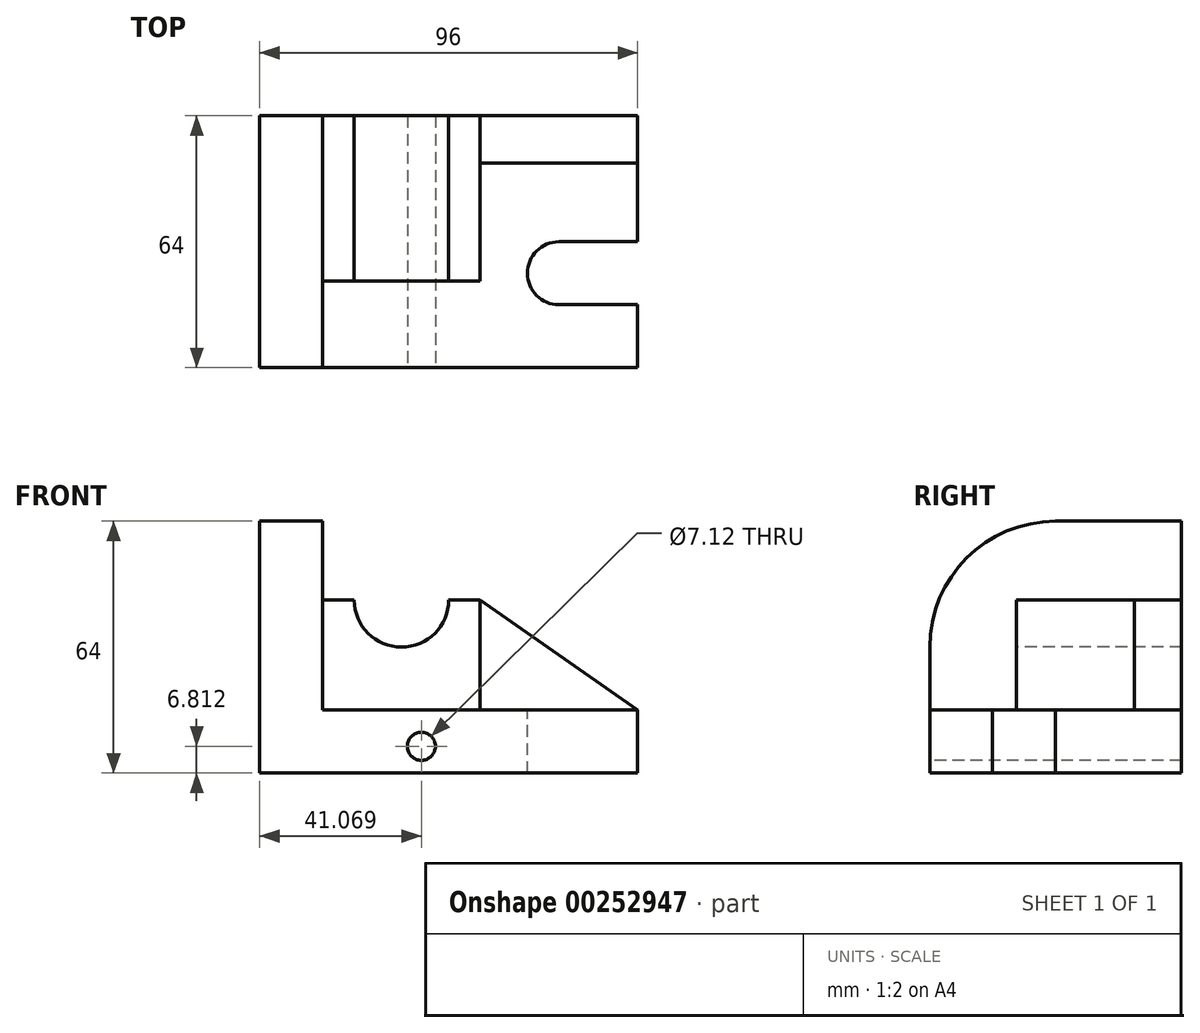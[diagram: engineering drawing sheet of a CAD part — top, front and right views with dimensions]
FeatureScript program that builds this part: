
annotation { "Feature Type Name" : "Feature", "Feature Type Description" : "" }
export const myFeature = defineFeature(function(context is Context, id is Id, definition is map)
    precondition{}
    {
        {
            var Q0;
            Q0=qCreatedBy(makeId("Top.planeOp"),FACE);
            var sketch = newSketch(context, id + "F0", { "sketchPlane" : qUnion([Q0])});
            skLineSegment(sketch, "E0.bottom", {"start": v(0, 0) * mm, "end": v(96, 0) * mm});
            skLineSegment(sketch, "E0.top", {"start": v(0, 64) * mm, "end": v(96, 64) * mm});
            skLineSegment(sketch, "E0.left", {"start": v(0, 0) * mm, "end": v(0, 64) * mm});
            skLineSegment(sketch, "E0.right", {"start": v(96, 0) * mm, "end": v(96, 64) * mm});
            skSolve(sketch);
        }
        {
            var Q0;
            Q0=makeQuery(id+"F0.imprint","IMPRINT",FACE,{"disambiguationData":[TD([[makeQuery(id+"F0.imprint","IMPRINT",EDGE,{"derivedFrom":sQuery(id+"F0.wireOp",EDGE,"E0.bottom")}),1.0]])]});
            extrude(context, id + "F1", {"entities" : qUnion([Q0]), "depth" : 16 * mm});
        }
        {
            var Q0;
            Q0=makeQuery(id+"F1.opExtrude","CAP_FACE",FACE,{"disambiguationData":[OSD([sQuery(id+"F0.wireOp",EDGE,"E0.bottom"),sQuery(id+"F0.wireOp",EDGE,"E0.top"),sQuery(id+"F0.wireOp",EDGE,"E0.left"),sQuery(id+"F0.wireOp",EDGE,"E0.right")])],"isStart":false});
            var sketch = newSketch(context, id + "F2", { "sketchPlane" : qUnion([Q0])});
            skLineSegment(sketch, "E1.0", {"start": v(76, 16) * mm, "end": v(96, 16) * mm});
            skLineSegment(sketch, "E2.0", {"start": v(76, 32) * mm, "end": v(96, 32) * mm});
            skArc(sketch, "E3", {"start": v(76, 32) * mm, "mid": v(68, 24) * mm, "end": v(76, 16) * mm});
            skLineSegment(sketch, "E4", {"start": v(96, 32) * mm, "end": v(96, 16) * mm});
            skSolve(sketch);
        }
        {
            var Q0;
            Q0=makeQuery(id+"F2.imprint","IMPRINT",FACE,{"disambiguationData":[TD([[makeQuery(id+"F2.imprint","IMPRINT",EDGE,{"derivedFrom":sQuery(id+"F2.wireOp",EDGE,"E1.0")}),1.0]])]});
            extrude(context, id + "F3", {"entities" : qUnion([Q0]), "operationType" : NewBodyOperationType.REMOVE, "endBound" : BoundingType.THROUGH_ALL, "oppositeDirection" : true, "depth" : 25.4 * mm});
        }
        {
            var Q0;
            Q0=makeQuery(id+"F1.opExtrude","CAP_FACE",FACE,{"disambiguationData":[OSD([sQuery(id+"F0.wireOp",EDGE,"E0.bottom"),sQuery(id+"F0.wireOp",EDGE,"E0.top"),sQuery(id+"F0.wireOp",EDGE,"E0.left"),sQuery(id+"F0.wireOp",EDGE,"E0.right")])],"isStart":false});
            var sketch = newSketch(context, id + "F4", { "sketchPlane" : qUnion([Q0])});
            skLineSegment(sketch, "E5.bottom", {"start": v(0, 0) * mm, "end": v(16, 0) * mm});
            skLineSegment(sketch, "E5.top", {"start": v(0, 64) * mm, "end": v(16, 64) * mm});
            skLineSegment(sketch, "E5.left", {"start": v(0, 0) * mm, "end": v(0, 64) * mm});
            skLineSegment(sketch, "E5.right", {"start": v(16, 0) * mm, "end": v(16, 64) * mm});
            skSolve(sketch);
        }
        {
            var Q0;
            Q0=makeQuery(id+"F4.imprint","IMPRINT",FACE,{"disambiguationData":[TD([[makeQuery(id+"F4.imprint","IMPRINT",EDGE,{"derivedFrom":sQuery(id+"F4.wireOp",EDGE,"E5.bottom")}),1.0]])]});
            extrude(context, id + "F5", {"entities" : qUnion([Q0]), "operationType" : NewBodyOperationType.ADD, "depth" : 48 * mm});
        }
        {
            var Q0;
            Q0=makeQuery(id+"F5.opExtrude","CAP_EDGE",EDGE,{"disambiguationData":[OSD([sQuery(id+"F4.wireOp",EDGE,"E5.bottom")])],"isStart":false});
            fillet(context, id + "F6", {"entities" : qUnion([Q0]), "radius" : 32 * mm, "tangentPropagation" : true, "allowEdgeOverflow" : false});
        }
        {
            var Q0;
            Q0=makeQuery(id+"F1.opExtrude","CAP_FACE",FACE,{"disambiguationData":[OSD([sQuery(id+"F0.wireOp",EDGE,"E0.bottom"),sQuery(id+"F0.wireOp",EDGE,"E0.top"),sQuery(id+"F0.wireOp",EDGE,"E0.left"),sQuery(id+"F0.wireOp",EDGE,"E0.right")])],"isStart":false});
            var sketch = newSketch(context, id + "F7", { "sketchPlane" : qUnion([Q0])});
            skLineSegment(sketch, "E6.bottom", {"start": v(16, 64) * mm, "end": v(56, 64) * mm});
            skLineSegment(sketch, "E6.top", {"start": v(16, 22) * mm, "end": v(56, 22) * mm});
            skLineSegment(sketch, "E6.left", {"start": v(16, 64) * mm, "end": v(16, 22) * mm});
            skLineSegment(sketch, "E6.right", {"start": v(56, 64) * mm, "end": v(56, 22) * mm});
            skSolve(sketch);
        }
        {
            var Q0;
            Q0=makeQuery(id+"F7.imprint","IMPRINT",FACE,{"disambiguationData":[TD([[makeQuery(id+"F7.imprint","IMPRINT",EDGE,{"derivedFrom":sQuery(id+"F7.wireOp",EDGE,"E6.bottom")}),-1.0]])]});
            extrude(context, id + "F8", {"entities" : qUnion([Q0]), "operationType" : NewBodyOperationType.ADD, "depth" : 28 * mm});
        }
        {
            var Q0;
            Q0=makeQuery(id+"F8.opExtrude","SWEPT_FACE",FACE,{"disambiguationData":[OSD([sQuery(id+"F7.wireOp",EDGE,"E6.top")])]});
            var sketch = newSketch(context, id + "F9", { "sketchPlane" : qUnion([Q0])});
            skCircle(sketch, "E7", {"center": v(36, 44) * mm, "radius": 12 * mm});
            skSolve(sketch);
        }
        {
            var Q0;
            {var subQ0=sQuery(id+"F9.wireOp",EDGE,"E7");var subQ1=makeQuery(id+"F8.opExtrude","CAP_EDGE",EDGE,{"disambiguationData":[OSD([sQuery(id+"F7.wireOp",EDGE,"E6.top")])],"isStart":false});var subQ2=makeQuery(id+"F9.imprint","INTERSECT",VERTEX,{"disambiguationData":[OD(0.0)],"derivedFrom":[subQ1,subQ0]});Q0=makeQuery(id+"F9.imprint","IMPRINT",FACE,{"disambiguationData":[TD([[makeQuery(id+"F9.imprint","IMPRINT",EDGE,{"disambiguationData":[TD([[subQ2,-1.0]])],"derivedFrom":subQ0}),1.0]])]});}
            var Q1;
            {var subQ0=sQuery(id+"F9.wireOp",EDGE,"E7");var subQ1=makeQuery(id+"F8.opExtrude","CAP_EDGE",EDGE,{"disambiguationData":[OSD([sQuery(id+"F7.wireOp",EDGE,"E6.top")])],"isStart":false});var subQ2=makeQuery(id+"F9.imprint","INTERSECT",VERTEX,{"disambiguationData":[OD(0.0)],"derivedFrom":[subQ1,subQ0]});Q1=makeQuery(id+"F9.imprint","IMPRINT",FACE,{"disambiguationData":[TD([[makeQuery(id+"F9.imprint","IMPRINT",EDGE,{"disambiguationData":[TD([[subQ2,1.0]])],"derivedFrom":subQ0}),1.0]])]});}
            extrude(context, id + "F10", {"entities" : qUnion([Q0, Q1]), "operationType" : NewBodyOperationType.REMOVE, "endBound" : BoundingType.THROUGH_ALL, "oppositeDirection" : true, "depth" : 25.4 * mm});
        }
        {
            var Q0;
            Q0=makeQuery(id+"F8.boolean.opBoolean","MERGE",FACE,{"derivedFrom":[makeQuery(id+"F5.boolean.opBoolean","MERGE",FACE,{"derivedFrom":[makeQuery(id+"F1.opExtrude","SWEPT_FACE",FACE,{"disambiguationData":[OSD([sQuery(id+"F0.wireOp",EDGE,"E0.top")])]}),makeQuery(id+"F5.opExtrude","SWEPT_FACE",FACE,{"disambiguationData":[OSD([sQuery(id+"F4.wireOp",EDGE,"E5.top")])]})]}),makeQuery(id+"F8.opExtrude","SWEPT_FACE",FACE,{"disambiguationData":[OSD([sQuery(id+"F7.wireOp",EDGE,"E6.bottom")])]})]});
            var sketch = newSketch(context, id + "F11", { "sketchPlane" : qUnion([Q0])});
            skLineSegment(sketch, "E8", {"start": v(-56, 44) * mm, "end": v(-96, 16) * mm});
            skLineSegment(sketch, "E9", {"start": v(-96, 16) * mm, "end": v(-56, 16) * mm});
            skLineSegment(sketch, "E10", {"start": v(-56, 16) * mm, "end": v(-56, 44) * mm});
            skSolve(sketch);
        }
        {
            var Q0;
            Q0=makeQuery(id+"F11.imprint","IMPRINT",FACE,{"disambiguationData":[TD([[makeQuery(id+"F11.imprint","IMPRINT",EDGE,{"derivedFrom":sQuery(id+"F11.wireOp",EDGE,"E8")}),1.0]])]});
            extrude(context, id + "F12", {"entities" : qUnion([Q0]), "operationType" : NewBodyOperationType.ADD, "oppositeDirection" : true, "depth" : 12 * mm});
        }
        {
            var Q0;
            Q0=makeQuery(id+"F5.boolean.opBoolean","MERGE",FACE,{"derivedFrom":[makeQuery(id+"F1.opExtrude","SWEPT_FACE",FACE,{"disambiguationData":[OSD([sQuery(id+"F0.wireOp",EDGE,"E0.bottom")])]}),makeQuery(id+"F5.opExtrude","SWEPT_FACE",FACE,{"disambiguationData":[OSD([sQuery(id+"F4.wireOp",EDGE,"E5.bottom")])]})]});
            var sketch = newSketch(context, id + "F13", { "sketchPlane" : qUnion([Q0])});
            skCircle(sketch, "E11", {"center": v(41.07, 6.81) * mm, "radius": 3.56 * mm});
            skSolve(sketch);
        }
        {
            var Q0;
            Q0=makeQuery(id+"F13.imprint","IMPRINT",FACE,{"disambiguationData":[TD([[makeQuery(id+"F13.imprint","IMPRINT",EDGE,{"derivedFrom":sQuery(id+"F13.wireOp",EDGE,"E11")}),1.0]])]});
            extrude(context, id + "F14", {"entities" : qUnion([Q0]), "operationType" : NewBodyOperationType.REMOVE, "endBound" : BoundingType.THROUGH_ALL, "oppositeDirection" : true, "depth" : 25.4 * mm});
        }
    });
